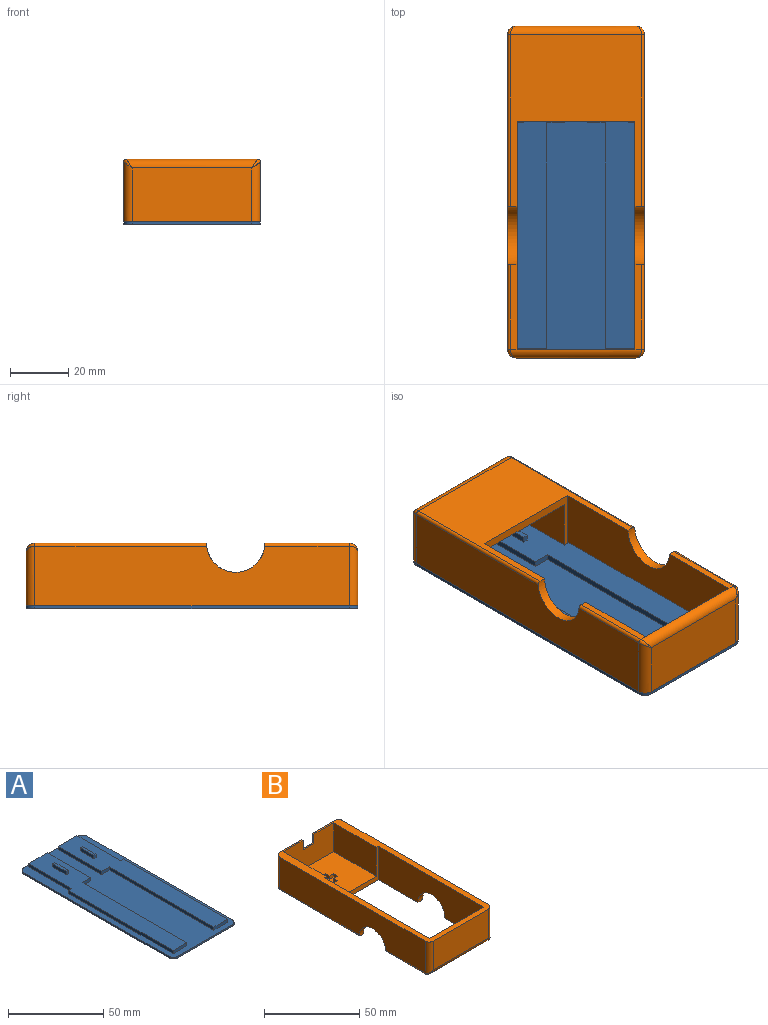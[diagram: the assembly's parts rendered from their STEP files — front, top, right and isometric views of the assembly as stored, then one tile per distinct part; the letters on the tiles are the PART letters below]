
ASSEMBLY  parts=2 mates=1
PART A: 38 faces, bbox 47x114x5 mm
  f0: plane 10.25x2mm, normal (0,-1,0), area 20.5mm2, adj f1,f7,f14,f27
  f1: plane 109.65x16.25mm, normal (0,0,1), area 1228.5mm2, adj f0,f2,f12,f13,f14,f25,f26,f27
  f2: plane 14x2mm, normal (0,1,0), area 28mm2, adj f1,f7,f12,f25
  f3: plane 108x1mm, normal (-1,0,0), area 108mm2, adj f7,f8,f18,f21
  f4: plane 41x1mm, normal (0,-1,0), area 41mm2, adj f7,f8,f18,f19
  f5: plane 108x1mm, normal (1,0,0), area 108mm2, adj f7,f8,f19,f20
  f6: plane 41x1mm, normal (0,1,0), area 41mm2, adj f7,f8,f20,f21
  f7: plane 114x47mm, normal (0,0,1), area 2861.3mm2, adj f0,f2,f3,f4,f5,f6,f10,f11
  f8: plane 114x47mm, normal (0,0,-1), area 5350.3mm2, adj f3,f4,f5,f6,f18,f19,f20,f21
  f9: plane 109.65x16.25mm, normal (0,0,1), area 1228.5mm2, adj f10,f11,f15,f16,f17,f22,f23,f24
  f10: plane 32.15x2mm, normal (1,0,0), area 64.3mm2, adj f7,f9,f11,f17
  f11: plane 14x2mm, normal (0,1,0), area 28mm2, adj f7,f9,f10,f24
  f12: plane 32.15x2mm, normal (-1,0,0), area 64.3mm2, adj f1,f2,f7,f13
  f13: plane 2.25x2mm, normal (0,1,0), area 4.5mm2, adj f1,f7,f12,f14
  f14: plane 77.5x2mm, normal (-1,0,0), area 155mm2, adj f0,f1,f7,f13
  f15: plane 10.25x2mm, normal (0,-1,0), area 20.5mm2, adj f7,f9,f16,f22
  f16: plane 77.5x2mm, normal (1,0,0), area 155mm2, adj f7,f9,f15,f17
  f17: plane 2.25x2mm, normal (0,1,0), area 4.5mm2, adj f7,f9,f10,f16
  f18: cylinder r=3mm len=3mm, axis (0,0,-1), area 4.7mm2, adj f3,f4,f7,f8
  f19: cylinder r=3mm len=3mm, axis (0,0,1), area 4.7mm2, adj f4,f5,f7,f8
  f20: cylinder r=3mm len=3mm, axis (0,0,-1), area 4.7mm2, adj f5,f6,f7,f8
  f21: cylinder r=3mm len=3mm, axis (0,0,1), area 4.7mm2, adj f3,f6,f7,f8
  f22: plane 77.5x2mm, normal (-1,0,0), area 155mm2, adj f7,f9,f15,f23
  f23: plane 6x2mm, normal (0,-1,0), area 12mm2, adj f7,f9,f22,f24
  f24: plane 32.15x2mm, normal (-1,0,0), area 64.3mm2, adj f7,f9,f11,f23
  f25: plane 32.15x2mm, normal (1,0,0), area 64.3mm2, adj f1,f2,f7,f26
  f26: plane 6x2mm, normal (0,-1,0), area 12mm2, adj f1,f7,f25,f27
  f27: plane 77.5x2mm, normal (1,0,0), area 155mm2, adj f0,f1,f7,f26
  f28: plane 10x2mm, normal (1,0,0), area 20mm2, adj f1,f29,f31,f32
  f29: plane 2x1.6mm, normal (0,1,0), area 3.2mm2, adj f1,f28,f30,f32
  f30: plane 10x2mm, normal (-1,0,0), area 20mm2, adj f1,f29,f31,f32
  f31: plane 2x1.6mm, normal (0,-1,0), area 3.2mm2, adj f1,f28,f30,f32
  f32: plane 10x1.6mm, normal (0,0,1), area 16mm2, adj f28,f29,f30,f31
  f33: plane 10x2mm, normal (1,0,0), area 20mm2, adj f9,f34,f36,f37
  f34: plane 2x1.6mm, normal (0,1,0), area 3.2mm2, adj f9,f33,f35,f37
  f35: plane 10x2mm, normal (-1,0,0), area 20mm2, adj f9,f34,f36,f37
  f36: plane 2x1.6mm, normal (0,-1,0), area 3.2mm2, adj f9,f33,f35,f37
  f37: plane 10x1.6mm, normal (0,0,1), area 16mm2, adj f33,f34,f35,f36
PART B: 48 faces, bbox 47x114x21.5 mm
  f0: plane 37.25x31.85mm, normal (0,0,1), area 1141.4mm2, adj f10,f11,f12,f13,f35,f36,f37,f38
  f1: plane 114x47mm, normal (0,0,1), area 987.5mm2, adj f4,f5,f6,f7,f8,f9,f10,f11
  f2: plane 29x2.25mm, normal (0,0,-1), area 65.2mm2, adj f7,f17,f19,f28
  f3: plane 59x45mm, normal (0,0,-1), area 1470.4mm2, adj f7,f9,f10,f16,f17,f22,f24,f26
  f4: plane 108x20.5mm, normal (-1,0,0), area 2076.9mm2, adj f1,f16,f20,f21,f26,f30
  f5: plane 41x18.5mm, normal (0,-1,0), area 758.5mm2, adj f1,f18,f19,f20
  f6: plane 108x20.5mm, normal (1,0,0), area 2076.9mm2, adj f1,f17,f18,f23,f24,f28
  f7: plane 78.25x21.5mm, normal (-1,0,0), area 1525.3mm2, adj f1,f2,f3,f8,f10,f17
  f8: plane 40.5x21.5mm, normal (0,1,0), area 870.8mm2, adj f1,f7,f9,f19
  f9: plane 78.25x21.5mm, normal (1,0,0), area 1525.3mm2, adj f1,f3,f8,f10,f15,f16
  f10: plane 40.5x21.5mm, normal (0,-1,0), area 181.6mm2, adj f0,f1,f3,f7,f9,f11,f13
  f11: plane 31.85x18.5mm, normal (1,0,0), area 589.2mm2, adj f0,f1,f10,f12
  f12: plane 37.25x18.5mm, normal (0,-1,0), area 641.1mm2, adj f0,f1,f11,f13,f32,f33,f34
  f13: plane 31.85x18.5mm, normal (-1,0,0), area 589.2mm2, adj f0,f1,f10,f12
  f14: plane 41x18.5mm, normal (0,1,0), area 710.5mm2, adj f1,f21,f22,f23,f32,f33,f34
  f15: plane 29x2.25mm, normal (0,0,-1), area 65.2mm2, adj f9,f16,f19,f30
  f16: cylinder r=10mm len=20mm, axis (1,0,0), area 101.7mm2, adj f3,f4,f9,f15,f26,f30
  f17: cylinder r=10mm len=20mm, axis (1,0,0), area 101.7mm2, adj f2,f3,f6,f7,f24,f28
  f18: cylinder r=3mm len=20.5mm, axis (0,0,1), area 93.2mm2, adj f1,f5,f6,f29
  f19: cylinder r=3mm len=45mm, axis (1,0,0), area 205.2mm2, adj f2,f5,f8,f15,f29,f31
  f20: cylinder r=3mm len=20.5mm, axis (0,0,-1), area 93.2mm2, adj f1,f4,f5,f31
  f21: cylinder r=3mm len=20.5mm, axis (0,0,1), area 93.2mm2, adj f1,f4,f14,f27
  f22: cylinder r=3mm len=45mm, axis (-1,0,0), area 205.2mm2, adj f3,f14,f25,f27
  f23: cylinder r=3mm len=20.5mm, axis (0,0,-1), area 93.2mm2, adj f1,f6,f14,f25
  f24: cylinder r=1mm len=59.05mm, axis (0,1,0), area 92.7mm2, adj f3,f6,f17,f25
  f25: bspline ~3.52x3mm, area 5mm2, adj f22,f23,f24
  f26: cylinder r=1mm len=59.05mm, axis (0,-1,0), area 92.7mm2, adj f3,f4,f16,f27
  f27: bspline ~3.52x3mm, area 5mm2, adj f21,f22,f26
  f28: cylinder r=1mm len=29.05mm, axis (0,1,0), area 45.6mm2, adj f2,f6,f17,f29
  f29: bspline ~3.52x3mm, area 5mm2, adj f18,f19,f28
  f30: cylinder r=1mm len=29.05mm, axis (0,-1,0), area 45.6mm2, adj f4,f15,f16,f31
  f31: bspline ~3.52x3mm, area 5mm2, adj f19,f20,f30
  f32: plane 6x0.9mm, normal (-1,0,0), area 5.4mm2, adj f1,f12,f14,f33
  f33: plane 8x0.9mm, normal (0,0,1), area 7.2mm2, adj f12,f14,f32,f34
  f34: plane 6x0.9mm, normal (1,0,0), area 5.4mm2, adj f1,f12,f14,f33
  f35: plane 3x2mm, normal (1,0,0), area 6mm2, adj f0,f36,f46,f47
  f36: plane 3x2mm, normal (0,1,0), area 6mm2, adj f0,f35,f37,f47
  f37: plane 3x2mm, normal (1,0,0), area 6mm2, adj f0,f36,f38,f47
  f38: plane 3x2mm, normal (0,1,0), area 6mm2, adj f0,f37,f39,f47
  f39: plane 3x2mm, normal (-1,0,0), area 6mm2, adj f0,f38,f40,f47
  f40: plane 3x2mm, normal (0,1,0), area 6mm2, adj f0,f39,f41,f47
  f41: plane 3x2mm, normal (-1,0,0), area 6mm2, adj f0,f40,f42,f47
  f42: plane 3x2mm, normal (0,-1,0), area 6mm2, adj f0,f41,f43,f47
  f43: plane 3x2mm, normal (-1,0,0), area 6mm2, adj f0,f42,f44,f47
  f44: plane 3x2mm, normal (0,-1,0), area 6mm2, adj f0,f43,f45,f47
  f45: plane 3x2mm, normal (1,0,0), area 6mm2, adj f0,f44,f46,f47
  f46: plane 3x2mm, normal (0,-1,0), area 6mm2, adj f0,f35,f45,f47
  f47: plane 9x9mm, normal (0,0,1), area 45mm2, adj f35,f36,f37,f38,f39,f40,f41,f42
PLACE A t=(-32.62,-12.51,7.99)mm
PLACE B rot(axis=(0,1,0),180deg) t=(-32.62,-12.51,30.49)mm
MATE fastened B.f1 <-> A.f7  axis (0,0,-1) through (-32.62,-69.51,8.99)mm
